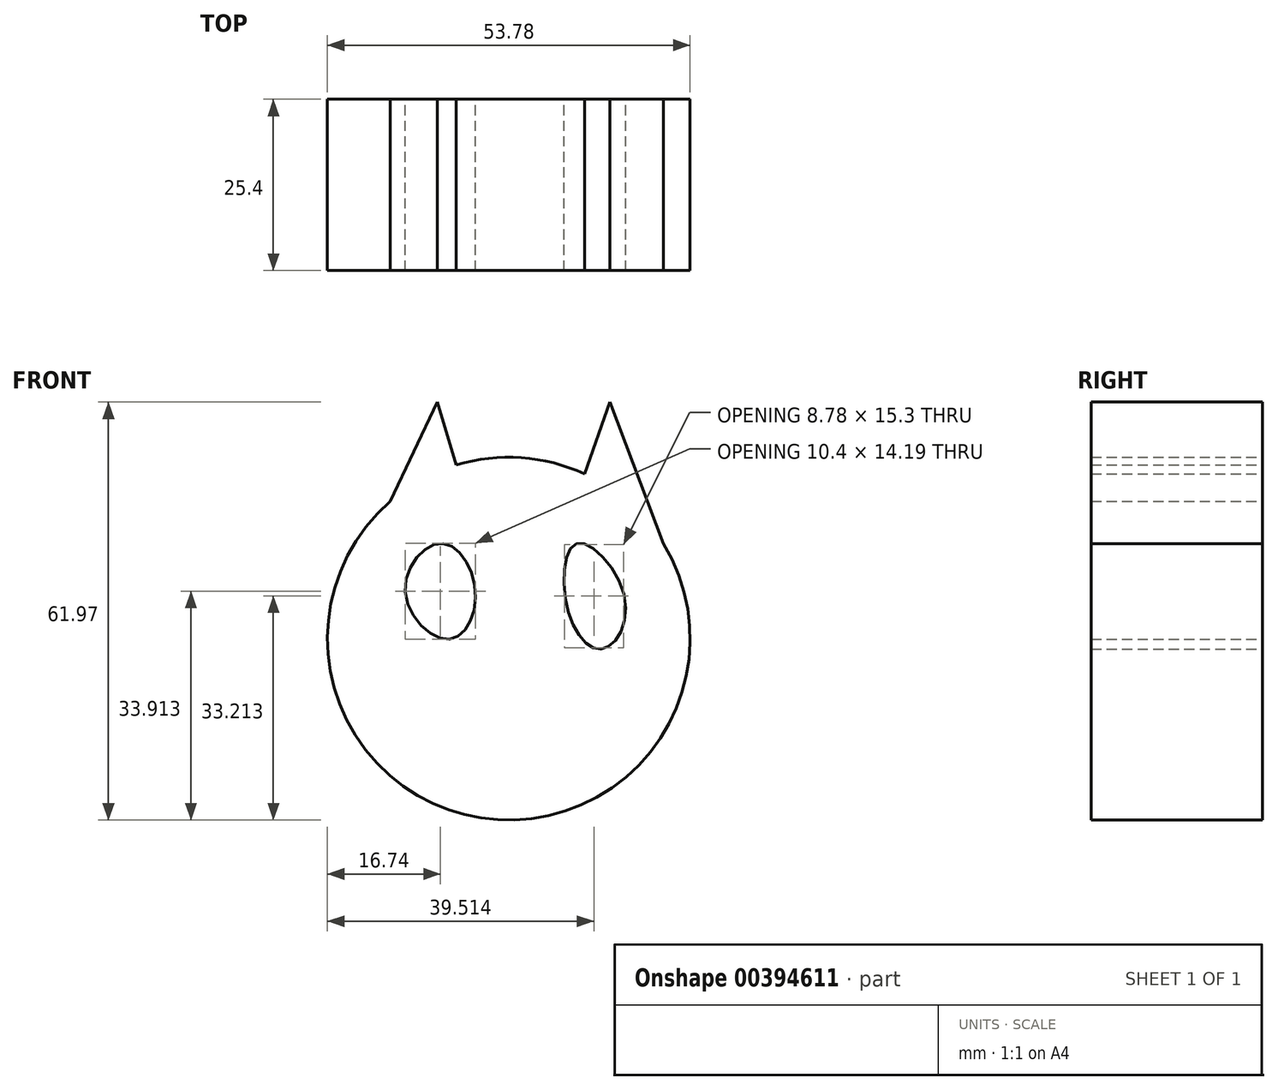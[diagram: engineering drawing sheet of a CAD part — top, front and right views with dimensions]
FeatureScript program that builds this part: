
annotation { "Feature Type Name" : "Feature", "Feature Type Description" : "" }
export const myFeature = defineFeature(function(context is Context, id is Id, definition is map)
    precondition{}
    {
        {
            var Q0;
            Q0=qCreatedBy(makeId("Front.planeOp"),FACE);
            var sketch = newSketch(context, id + "F0", { "sketchPlane" : qUnion([Q0])});
            skLineSegment(sketch, "E0", {"start": v(-48.35, 23.7) * mm, "end": v(-38.87, 43.8) * mm});
            skLineSegment(sketch, "E1", {"start": v(-32.8, 23.7) * mm, "end": v(-38.87, 43.8) * mm});
            skLineSegment(sketch, "E2", {"start": v(-20.29, 23.7) * mm, "end": v(-13.27, 43.8) * mm});
            skLineSegment(sketch, "E3", {"start": v(-6.26, 25.22) * mm, "end": v(-13.27, 43.8) * mm});
            skLineSegment(sketch, "E4", {"start": v(-6.26, 25.22) * mm, "end": v(-4.88, 21.56) * mm});
            skCircle(sketch, "E5", {"center": v(-28.25, 8.72) * mm, "radius": 26.89 * mm});
            skSolve(sketch);
        }
        {
            var Q0;
            Q0 = qSketchRegion(id + "F0", true);
            extrude(context, id + "F1", {"entities" : qUnion([Q0]), "depth" : 25.4 * mm});
        }
        {
            var Q0;
            Q0=makeQuery(id+"F1.opExtrude","CAP_FACE",FACE,{"disambiguationData":[OSD([sQuery(id+"F0.wireOp",EDGE,"E0"),sQuery(id+"F0.wireOp",EDGE,"E1"),sQuery(id+"F0.wireOp",EDGE,"E2"),sQuery(id+"F0.wireOp",EDGE,"E3"),sQuery(id+"F0.wireOp",EDGE,"E4"),sQuery(id+"F0.wireOp",EDGE,"E5")])],"isStart":false});
            var sketch = newSketch(context, id + "F2", { "sketchPlane" : qUnion([Q0])});
            skSolve(sketch);
        }
        {
            var Q0;
            {var subQ3=sQuery(id+"F0.wireOp",EDGE,"E0");Q0=makeQuery(id+"F2.imprint","IMPRINT",FACE,{"disambiguationData":[TD([[makeQuery(id+"F2.imprint","IMPRINT",EDGE,{"derivedFrom":makeQuery(id+"F1.opExtrude","CAP_EDGE",EDGE,{"disambiguationData":[OSD([subQ3])],"isStart":false})}),-1.0]])]});}
            var sketch = newSketch(context, id + "F3", { "sketchPlane" : qUnion([Q0])});
            skFitSpline(sketch, "E6", {"points": [v(-43.6, 15.67) * mm, v(-38.28, 22.84) * mm, v(-33.2, 15.67) * mm, v(-37.05, 8.66) * mm, v(-43.6, 15.67) * mm]});
            skFitSpline(sketch, "E7", {"points": [v(-19.4, 12.66) * mm, v(-18.09, 22.84) * mm, v(-11, 14.44) * mm, v(-14.39, 7.2) * mm, v(-19.4, 12.66) * mm]});
            skSolve(sketch);
        }
        {
            var Q0;
            Q0 = qSketchRegion(id + "F3", true);
            extrude(context, id + "F4", {"entities" : qUnion([Q0]), "operationType" : NewBodyOperationType.REMOVE, "depth" : 25.4 * mm, "hasSecondDirection" : true, "secondDirectionOppositeDirection" : true, "secondDirectionDepth" : 25.4 * mm});
        }
    });
